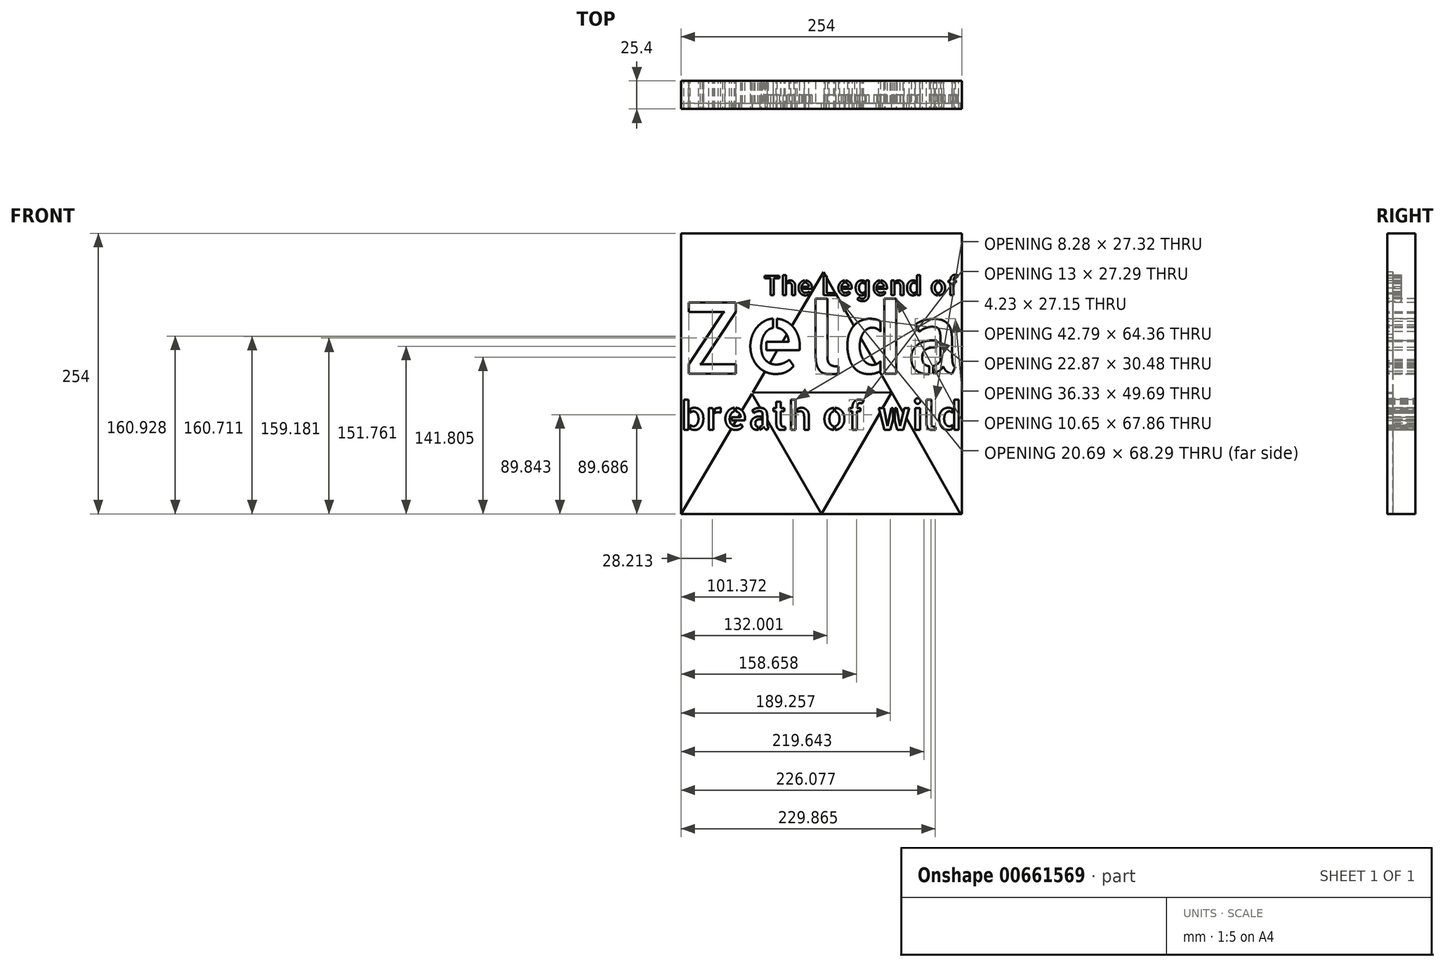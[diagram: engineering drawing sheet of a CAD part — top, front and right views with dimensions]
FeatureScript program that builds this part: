
annotation { "Feature Type Name" : "Feature", "Feature Type Description" : "" }
export const myFeature = defineFeature(function(context is Context, id is Id, definition is map)
    precondition{}
    {
        {
            var Q0;
            Q0=qCreatedBy(makeId("Front.planeOp"),FACE);
            var sketch = newSketch(context, id + "F0", { "sketchPlane" : qUnion([Q0])});
            skLineSegment(sketch, "E0.bottom", {"start": v(127, 127) * mm, "end": v(-127, 127) * mm});
            skLineSegment(sketch, "E0.top", {"start": v(127, -127) * mm, "end": v(-127, -127) * mm});
            skLineSegment(sketch, "E0.left", {"start": v(127, 127) * mm, "end": v(127, -127) * mm});
            skLineSegment(sketch, "E0.right", {"start": v(-127, 127) * mm, "end": v(-127, -127) * mm});
            skPoint(sketch, "E0.middle", {"position": v(0, 0) * mm});
            skSolve(sketch);
        }
        {
            var Q0;
            Q0 = qSketchRegion(id + "F0", true);
            extrude(context, id + "F1", {"entities" : qUnion([Q0]), "depth" : 25.4 * mm, "offsetDistance" : 25.4 * mm});
        }
        {
            var Q0;
            Q0=makeQuery(id+"F1.opExtrude","CAP_FACE",FACE,{"disambiguationData":[OSD([sQuery(id+"F0.wireOp",EDGE,"E0.bottom"),sQuery(id+"F0.wireOp",EDGE,"E0.top"),sQuery(id+"F0.wireOp",EDGE,"E0.left"),sQuery(id+"F0.wireOp",EDGE,"E0.right")])],"isStart":false});
            var sketch = newSketch(context, id + "F2", { "sketchPlane" : qUnion([Q0])});
            skText(sketch, "E1", { "text": "Zelda", "fontName": "AllertaStencil-Regular.ttf"});
            const initialGuessF2  = {"E1": [-0.127, 0, 1, 0, 0.06439]};
            skSetInitialGuess(sketch, initialGuessF2);
            skSolve(sketch);
        }
        {
            var Q0;
            Q0 = qSketchRegion(id + "F2", true);
            extrude(context, id + "F3", {"entities" : qUnion([Q0]), "operationType" : NewBodyOperationType.REMOVE, "oppositeDirection" : true, "depth" : 25.4 * mm, "offsetDistance" : 25.4 * mm});
        }
        {
            var Q0;
            Q0=qCreatedBy(makeId("Front.planeOp"),FACE);
            var sketch = newSketch(context, id + "F4", { "sketchPlane" : qUnion([Q0])});
            skText(sketch, "E2", { "text": "breath of wild", "fontName": "AllertaStencil-Regular.ttf"});
            const initialGuessF4  = {"E2": [-0.1275, -0.0508, 1, 0, 0.02576]};
            skSetInitialGuess(sketch, initialGuessF4);
            skSolve(sketch);
        }
        {
            var Q0;
            Q0=makeQuery(id+"F1.opExtrude","CAP_FACE",FACE,{"disambiguationData":[OSD([sQuery(id+"F0.wireOp",EDGE,"E0.bottom"),sQuery(id+"F0.wireOp",EDGE,"E0.top"),sQuery(id+"F0.wireOp",EDGE,"E0.left"),sQuery(id+"F0.wireOp",EDGE,"E0.right")])],"isStart":false});
            var sketch = newSketch(context, id + "F5", { "sketchPlane" : qUnion([Q0])});
            skText(sketch, "E3", { "text": "The Legend of", "fontName": "AllertaStencil-Regular.ttf"});
            const initialGuessF5  = {"E3": [-0.05259, 0.0709, 1, 0, 0.01745]};
            skSetInitialGuess(sketch, initialGuessF5);
            skSolve(sketch);
        }
        {
            var Q0;
            Q0=makeQuery(id+"F1.opExtrude","CAP_FACE",FACE,{"disambiguationData":[OSD([sQuery(id+"F0.wireOp",EDGE,"E0.bottom"),sQuery(id+"F0.wireOp",EDGE,"E0.top"),sQuery(id+"F0.wireOp",EDGE,"E0.left"),sQuery(id+"F0.wireOp",EDGE,"E0.right")])],"isStart":false});
            var sketch = newSketch(context, id + "F6", { "sketchPlane" : qUnion([Q0])});
            skCircle(sketch, "E4.cCircle", {"center": v(-63.2, -90.86) * mm, "radius": 36.66 * mm, "construction": true});
            skLineSegment(sketch, "E4.0", {"start": v(0, -128.03) * mm, "end": v(-127, -127) * mm});
            skLineSegment(sketch, "E4.1", {"start": v(-127, -127) * mm, "end": v(-62.6, -17.53) * mm});
            skLineSegment(sketch, "E4.2", {"start": v(-62.6, -17.53) * mm, "end": v(0, -128.03) * mm});
            skPoint(sketch, "E4.0.midPoint", {"position": v(-63.5, -127.52) * mm});
            skCircle(sketch, "E5.cCircle", {"center": v(63.2, -90.86) * mm, "radius": 36.66 * mm, "construction": true});
            skLineSegment(sketch, "E5.0", {"start": v(126.4, -128.03) * mm, "end": v(-0.59, -127) * mm});
            skLineSegment(sketch, "E5.1", {"start": v(-0.59, -127) * mm, "end": v(63.8, -17.53) * mm});
            skLineSegment(sketch, "E5.2", {"start": v(63.8, -17.53) * mm, "end": v(126.4, -128.03) * mm});
            skCircle(sketch, "E6.cCircle", {"center": v(1.19, 18.61) * mm, "radius": 36.66 * mm, "construction": true});
            skLineSegment(sketch, "E6.0", {"start": v(64.39, -18.57) * mm, "end": v(-62.6, -17.53) * mm});
            skLineSegment(sketch, "E6.1", {"start": v(-62.6, -17.53) * mm, "end": v(1.78, 91.93) * mm});
            skLineSegment(sketch, "E6.2", {"start": v(1.78, 91.93) * mm, "end": v(64.39, -18.57) * mm});
            skSolve(sketch);
        }
        {
            var Q0;
            Q0 = qSketchRegion(id + "F6", true);
            extrude(context, id + "F7", {"entities" : qUnion([Q0]), "operationType" : NewBodyOperationType.REMOVE, "oppositeDirection" : true, "depth" : 5.08 * mm, "offsetDistance" : 25.4 * mm});
        }
        {
            var Q0;
            Q0=makeQuery(id+"F1.opExtrude","CAP_FACE",FACE,{"disambiguationData":[OSD([sQuery(id+"F0.wireOp",EDGE,"E0.bottom"),sQuery(id+"F0.wireOp",EDGE,"E0.top"),sQuery(id+"F0.wireOp",EDGE,"E0.left"),sQuery(id+"F0.wireOp",EDGE,"E0.right")])],"isStart":true});
            var sketch = newSketch(context, id + "F8", { "sketchPlane" : qUnion([Q0])});
            skCircle(sketch, "E7.cCircle", {"center": v(0.12, -53.68) * mm, "radius": 36.66 * mm, "construction": true});
            skLineSegment(sketch, "E7.0", {"start": v(0, -127) * mm, "end": v(-63.33, -16.92) * mm});
            skLineSegment(sketch, "E7.1", {"start": v(-63.33, -16.92) * mm, "end": v(63.67, -17.11) * mm});
            skLineSegment(sketch, "E7.2", {"start": v(63.67, -17.11) * mm, "end": v(0, -127) * mm});
            skPoint(sketch, "E7.0.midPoint", {"position": v(-31.66, -71.96) * mm});
            skSolve(sketch);
        }
        {
            var Q0;
            Q0 = qSketchRegion(id + "F8", true);
            extrude(context, id + "F9", {"entities" : qUnion([Q0]), "operationType" : NewBodyOperationType.ADD, "oppositeDirection" : true, "depth" : 25.4 * mm, "offsetDistance" : 25.4 * mm});
        }
        {
            var Q0;
            Q0 = qSketchRegion(id + "F5", true);
            extrude(context, id + "F10", {"entities" : qUnion([Q0]), "operationType" : NewBodyOperationType.REMOVE, "oppositeDirection" : true, "depth" : 12.7 * mm, "offsetDistance" : 25.4 * mm});
        }
        {
            var Q0;
            Q0 = qSketchRegion(id + "F4", true);
            extrude(context, id + "F11", {"entities" : qUnion([Q0]), "operationType" : NewBodyOperationType.REMOVE, "depth" : 25.4 * mm, "offsetDistance" : 25.4 * mm});
        }
    });
